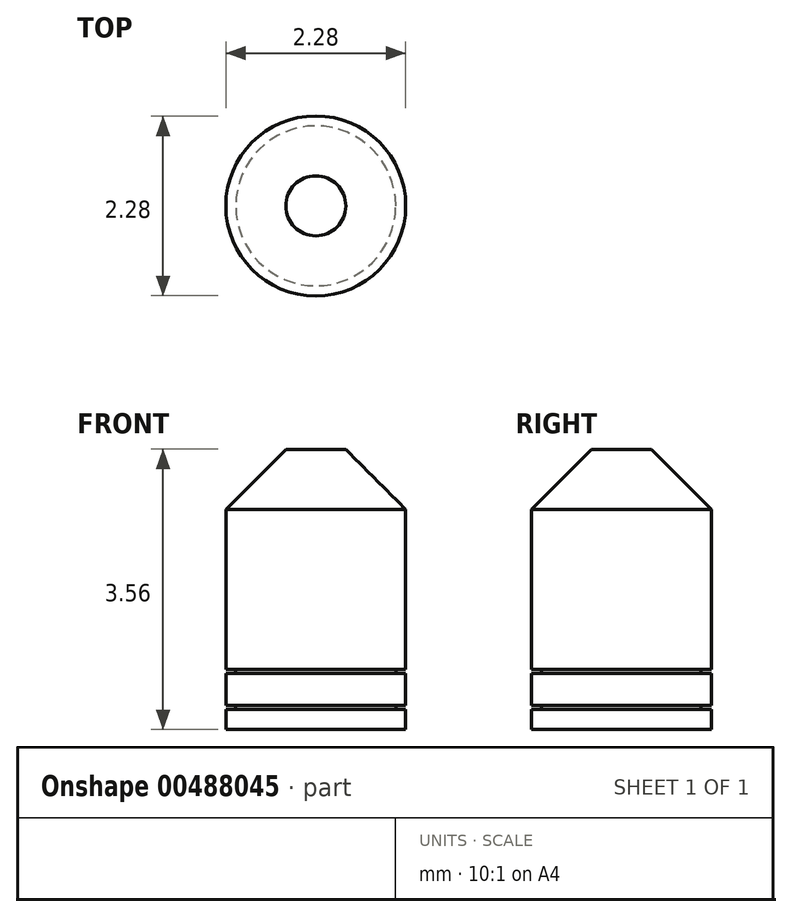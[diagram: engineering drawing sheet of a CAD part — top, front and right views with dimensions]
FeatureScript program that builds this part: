
annotation { "Feature Type Name" : "Feature", "Feature Type Description" : "" }
export const myFeature = defineFeature(function(context is Context, id is Id, definition is map)
    precondition{}
    {
        {
            var Q0;
            Q0=qCreatedBy(makeId("Top.planeOp"),FACE);
            var sketch = newSketch(context, id + "F0", { "sketchPlane" : qUnion([Q0])});
            skCircle(sketch, "E0", {"center": v(0, 0) * mm, "radius": 1.14 * mm});
            skSolve(sketch);
        }
        {
            var Q0;
            Q0 = qSketchRegion(id + "F0", true);
            extrude(context, id + "F1", {"entities" : qUnion([Q0]), "depth" : 3.56 * mm, "offsetDistance" : 25.4 * mm});
        }
        {
            var Q0;
            Q0=qCreatedBy(makeId("Top.planeOp"),FACE);
            cPlane(context, id + "F2", {"entities" : qUnion([Q0]), "cplaneType" : CPlaneType.OFFSET, "offset" : 0.25 * mm, "width" : 152.4 * mm, "height" : 152.4 * mm});
        }
        {
            var Q0;
            Q0=qCreatedBy(id+"F2.planeOp",FACE);
            cPlane(context, id + "F3", {"entities" : qUnion([Q0]), "cplaneType" : CPlaneType.OFFSET, "offset" : 0.5 * mm, "width" : 152.4 * mm, "height" : 152.4 * mm});
        }
        {
            var Q0;
            Q0=qCreatedBy(id+"F2.planeOp",FACE);
            var sketch = newSketch(context, id + "F4", { "sketchPlane" : qUnion([Q0])});
            skCircle(sketch, "E1", {"center": v(0, 0) * mm, "radius": 1.02 * mm});
            skCircle(sketch, "E2", {"center": v(0, 0) * mm, "radius": 1.16 * mm});
            skSolve(sketch);
        }
        {
            var Q0;
            Q0 = qSketchRegion(id + "F4", true);
            extrude(context, id + "F5", {"entities" : qUnion([Q0]), "operationType" : NewBodyOperationType.REMOVE, "depth" : 0.05 * mm, "offsetDistance" : 25.4 * mm});
        }
        {
            var Q0;
            Q0=qCreatedBy(id+"F3.planeOp",FACE);
            var sketch = newSketch(context, id + "F6", { "sketchPlane" : qUnion([Q0])});
            skCircle(sketch, "E3", {"center": v(0, 0) * mm, "radius": 1.16 * mm});
            skCircle(sketch, "E4", {"center": v(0, 0) * mm, "radius": 1.02 * mm});
            skSolve(sketch);
        }
        {
            var Q0;
            Q0 = qSketchRegion(id + "F6", true);
            extrude(context, id + "F7", {"entities" : qUnion([Q0]), "operationType" : NewBodyOperationType.REMOVE, "oppositeDirection" : true, "depth" : 0.05 * mm, "offsetDistance" : 25.4 * mm});
        }
        {
            var Q0;
            Q0=makeQuery(id+"F1.opExtrude","CAP_EDGE",EDGE,{"disambiguationData":[OSD([sQuery(id+"F0.wireOp",EDGE,"E0")])],"isStart":false});
            chamfer(context, id + "F8", {"entities" : qUnion([Q0]), "width" : 0.76 * mm, "tangentPropagation" : true});
        }
    });
